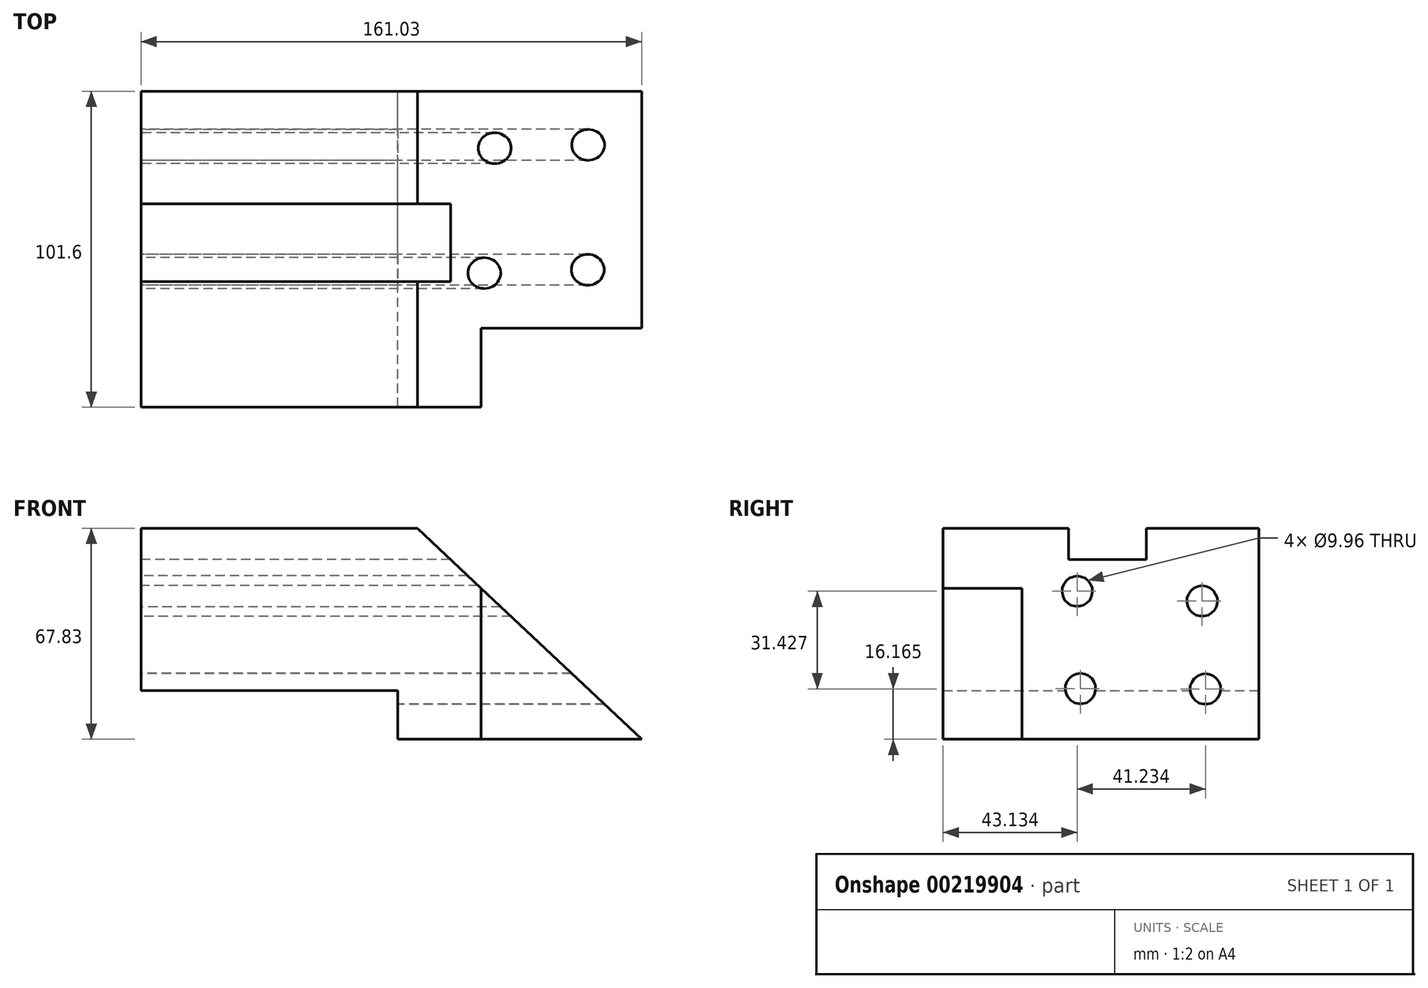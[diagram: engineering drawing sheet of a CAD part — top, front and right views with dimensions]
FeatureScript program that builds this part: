
annotation { "Feature Type Name" : "Feature", "Feature Type Description" : "" }
export const myFeature = defineFeature(function(context is Context, id is Id, definition is map)
    precondition{}
    {
        {
            var Q0;
            Q0=qCreatedBy(makeId("Front.planeOp"),FACE);
            var sketch = newSketch(context, id + "F0", { "sketchPlane" : qUnion([Q0])});
            skLineSegment(sketch, "E0", {"start": v(-99.46, -18.36) * mm, "end": v(-99.46, 23.38) * mm});
            skLineSegment(sketch, "E1", {"start": v(-99.46, 23.38) * mm, "end": v(-10.55, 23.38) * mm});
            skLineSegment(sketch, "E2", {"start": v(-10.55, 23.38) * mm, "end": v(9.96, 4.09) * mm});
            skLineSegment(sketch, "E3", {"start": v(9.96, 4.09) * mm, "end": v(9.96, -44.45) * mm});
            skLineSegment(sketch, "E4", {"start": v(9.96, -44.45) * mm, "end": v(-16.86, -44.45) * mm});
            skLineSegment(sketch, "E5", {"start": v(-16.86, -44.45) * mm, "end": v(-16.86, -28.75) * mm});
            skLineSegment(sketch, "E6", {"start": v(-16.86, -28.75) * mm, "end": v(-99.46, -28.75) * mm});
            skLineSegment(sketch, "E7", {"start": v(-99.46, -18.36) * mm, "end": v(-99.46, -28.75) * mm});
            skSolve(sketch);
        }
        {
            var Q0;
            Q0 = qSketchRegion(id + "F0", true);
            extrude(context, id + "F1", {"entities" : qUnion([Q0]), "depth" : 101.6 * mm});
        }
        {
            var Q0;
            Q0=makeQuery(id+"F1.opExtrude","CAP_FACE",FACE,{"disambiguationData":[OSD([sQuery(id+"F0.wireOp",EDGE,"E0"),sQuery(id+"F0.wireOp",EDGE,"E1"),sQuery(id+"F0.wireOp",EDGE,"E2"),sQuery(id+"F0.wireOp",EDGE,"E3"),sQuery(id+"F0.wireOp",EDGE,"E4"),sQuery(id+"F0.wireOp",EDGE,"E5"),sQuery(id+"F0.wireOp",EDGE,"E6"),sQuery(id+"F0.wireOp",EDGE,"E7")])],"isStart":true});
            var sketch = newSketch(context, id + "F2", { "sketchPlane" : qUnion([Q0])});
            skLineSegment(sketch, "E8", {"start": v(-9.96, 4.09) * mm, "end": v(-61.57, -44.45) * mm});
            skLineSegment(sketch, "E9", {"start": v(-61.57, -44.45) * mm, "end": v(-9.96, -44.45) * mm});
            skLineSegment(sketch, "E10", {"start": v(-9.96, -44.45) * mm, "end": v(-9.96, 4.09) * mm});
            skSolve(sketch);
        }
        {
            var Q0;
            Q0 = qSketchRegion(id + "F2", true);
            extrude(context, id + "F3", {"entities" : qUnion([Q0]), "operationType" : NewBodyOperationType.ADD, "oppositeDirection" : true, "depth" : 76.2 * mm});
        }
        {
            var Q0;
            Q0=makeQuery(id+"F1.opExtrude","SWEPT_FACE",FACE,{"disambiguationData":[OSD([sQuery(id+"F0.wireOp",EDGE,"E0"),sQuery(id+"F0.wireOp",EDGE,"E7")])]});
            var sketch = newSketch(context, id + "F4", { "sketchPlane" : qUnion([Q0])});
            skLineSegment(sketch, "E11.bottom", {"start": v(36.26, 13.34) * mm, "end": v(61.27, 13.34) * mm});
            skLineSegment(sketch, "E11.top", {"start": v(36.26, 33.42) * mm, "end": v(61.27, 33.42) * mm});
            skLineSegment(sketch, "E11.left", {"start": v(36.26, 13.34) * mm, "end": v(36.26, 33.42) * mm});
            skLineSegment(sketch, "E11.right", {"start": v(61.27, 13.34) * mm, "end": v(61.27, 33.42) * mm});
            skPoint(sketch, "E11.middle", {"position": v(48.76, 23.38) * mm});
            skSolve(sketch);
        }
        {
            var Q0;
            Q0 = qSketchRegion(id + "F4", true);
            extrude(context, id + "F5", {"entities" : qUnion([Q0]), "operationType" : NewBodyOperationType.REMOVE, "oppositeDirection" : true, "depth" : 103.38 * mm});
        }
        {
            var Q0;
            Q0=makeQuery(id+"F1.opExtrude","SWEPT_FACE",FACE,{"disambiguationData":[OSD([sQuery(id+"F0.wireOp",EDGE,"E0"),sQuery(id+"F0.wireOp",EDGE,"E7")])]});
            var sketch = newSketch(context, id + "F6", { "sketchPlane" : qUnion([Q0])});
            skCircle(sketch, "E12", {"center": v(18.29, 0) * mm, "radius": 4.98 * mm});
            skCircle(sketch, "E13", {"center": v(58.47, 3.14) * mm, "radius": 4.98 * mm});
            skCircle(sketch, "E14", {"center": v(17.23, -28.29) * mm, "radius": 4.98 * mm});
            skCircle(sketch, "E15", {"center": v(57.41, -28.17) * mm, "radius": 4.98 * mm});
            skSolve(sketch);
        }
        {
            var Q0;
            Q0=makeQuery(id+"F6.imprint","IMPRINT",FACE,{"disambiguationData":[TD([[makeQuery(id+"F6.imprint","IMPRINT",EDGE,{"derivedFrom":sQuery(id+"F6.wireOp",EDGE,"E12")}),1.0]])]});
            var Q1;
            Q1=makeQuery(id+"F6.imprint","IMPRINT",FACE,{"disambiguationData":[TD([[makeQuery(id+"F6.imprint","IMPRINT",EDGE,{"derivedFrom":sQuery(id+"F6.wireOp",EDGE,"E15")}),1.0]])]});
            var Q2;
            Q2=makeQuery(id+"F6.imprint","IMPRINT",FACE,{"disambiguationData":[TD([[makeQuery(id+"F6.imprint","IMPRINT",EDGE,{"derivedFrom":sQuery(id+"F6.wireOp",EDGE,"E13")}),1.0]])]});
            var Q3;
            Q3=makeQuery(id+"F6.imprint","IMPRINT",FACE,{"disambiguationData":[TD([[makeQuery(id+"F6.imprint","IMPRINT",EDGE,{"derivedFrom":sQuery(id+"F6.wireOp",EDGE,"E14")}),1.0]])]});
            extrude(context, id + "F7", {"entities" : qUnion([Q0, Q1, Q2, Q3]), "operationType" : NewBodyOperationType.REMOVE, "oppositeDirection" : true, "depth" : 167.13 * mm});
        }
    });
